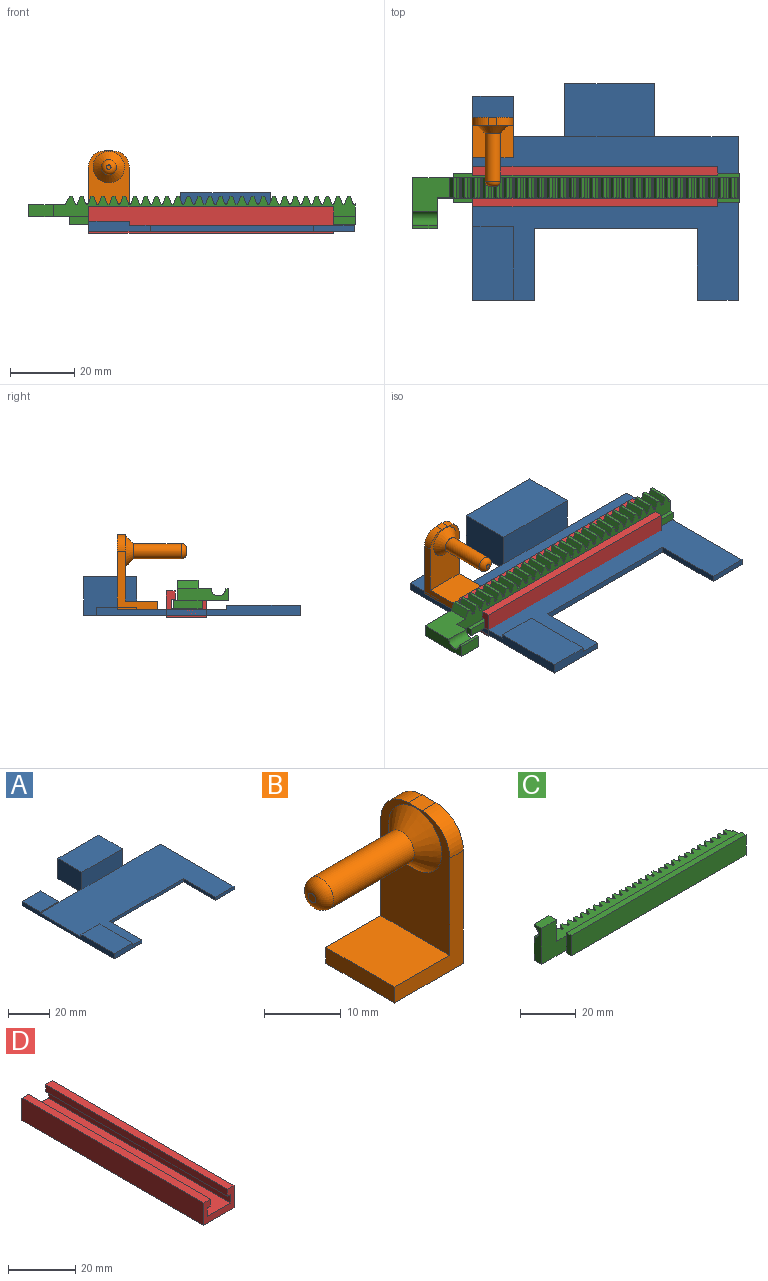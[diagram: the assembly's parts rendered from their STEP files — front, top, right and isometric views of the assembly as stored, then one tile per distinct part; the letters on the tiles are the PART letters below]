
ASSEMBLY  parts=4 mates=4
PART A: 23 faces, bbox 82.6x67.3x12.1 mm
  f0: plane 26.04x1.91mm, normal (0,1,0), area 49.6mm2, adj f2,f3,f15,f20
  f1: plane 19.05x3.18mm, normal (0,-1,0), area 52.4mm2, adj f2,f3,f5,f8,f9,f12
  f2: plane 82.55x50.8mm, normal (0,0,1), area 2774.2mm2, adj f0,f1,f4,f5,f6,f7,f8,f12
  f3: plane 82.55x67.31mm, normal (0,0,-1), area 3687.1mm2, adj f0,f1,f4,f5,f6,f10,f11,f12
  f4: plane 15.88x1.91mm, normal (0,1,0), area 30.2mm2, adj f2,f3,f10,f19
  f5: plane 63.5x3.18mm, normal (-1,0,0), area 158.1mm2, adj f1,f2,f3,f7,f9,f11,f16,f17
  f6: plane 12.7x1.91mm, normal (0,-1,0), area 24.2mm2, adj f2,f3,f13,f15
  f7: plane 12.7x1.27mm, normal (0,1,0), area 16.1mm2, adj f2,f5,f8,f9
  f8: plane 22.86x1.27mm, normal (1,0,0), area 29mm2, adj f1,f2,f7,f9
  f9: plane 22.86x12.7mm, normal (0,0,1), area 290.3mm2, adj f1,f5,f7,f8
  f10: plane 12.7x2.54mm, normal (1,0,0), area 32.3mm2, adj f3,f4,f11,f16,f17
  f11: plane 12.7x2.54mm, normal (0,1,0), area 32.3mm2, adj f3,f5,f10,f17
  f12: plane 22.23x1.91mm, normal (1,0,0), area 42.3mm2, adj f1,f2,f3,f14
  f13: plane 22.23x1.91mm, normal (-1,0,0), area 42.3mm2, adj f2,f3,f6,f14
  f14: plane 50.8x1.91mm, normal (0,-1,0), area 96.8mm2, adj f2,f3,f12,f13
  f15: plane 50.8x1.91mm, normal (1,0,0), area 96.8mm2, adj f0,f2,f3,f6
  f16: plane 12.7x0.64mm, normal (0,-1,0), area 8.1mm2, adj f2,f5,f10,f17
  f17: plane 12.7x12.7mm, normal (0,0,1), area 161.3mm2, adj f5,f10,f11,f16
  f18: plane 27.94x10.16mm, normal (0,-1,0), area 283.9mm2, adj f2,f19,f20,f22
  f19: plane 16.51x12.07mm, normal (-1,0,0), area 199.2mm2, adj f3,f4,f18,f21,f22
  f20: plane 16.51x12.07mm, normal (1,0,0), area 199.2mm2, adj f0,f3,f18,f21,f22
  f21: plane 27.94x12.07mm, normal (0,1,0), area 337.1mm2, adj f3,f19,f20,f22
  f22: plane 27.94x16.51mm, normal (0,0,1), area 461.3mm2, adj f18,f19,f20,f21
PART B: 14 faces, bbox 21.6x12.7x23.1 mm
  f0: plane 20.57x12.7mm, normal (-1,0,0), area 175.1mm2, adj f1,f5,f6,f7,f11,f12,f13
  f1: plane 12.7x10.16mm, normal (0,0,1), area 129mm2, adj f0,f2,f6,f7
  f2: plane 12.7x2.54mm, normal (-1,0,0), area 32.3mm2, adj f1,f3,f6,f7
  f3: plane 12.7x12.7mm, normal (0,0,-1), area 161.3mm2, adj f2,f4,f6,f7
  f4: plane 23.11x12.7mm, normal (1,0,0), area 282.5mm2, adj f3,f5,f6,f7,f11,f12
  f5: plane 2.54x2.54mm, normal (0,0,1), area 6.5mm2, adj f0,f4,f11,f12
  f6: plane 18.03x12.7mm, normal (0,-1,0), area 71.6mm2, adj f0,f1,f2,f3,f4,f12
  f7: plane 18.03x12.7mm, normal (0,1,0), area 71.6mm2, adj f0,f1,f2,f3,f4,f11
  f8: cylinder r=2.35mm len=14.86mm, axis (1,0,0), area 219.4mm2, adj f10,f13
  f9: plane 1.4x1.4mm, normal (-1,0,0), area 1.5mm2, adj f10
  f10: torus R=0.7mm, axis (-1,0,0), area 28.5mm2, adj f8,f9
  f11: cylinder r=5.08mm len=5.08mm, axis (-1,0,0), area 20.3mm2, adj f0,f4,f5,f7
  f12: cylinder r=5.08mm len=5.08mm, axis (1,0,0), area 20.3mm2, adj f0,f4,f5,f6
  f13: cone r=2.35mm half-angle=45deg, axis (1,0,0), area 81.7mm2, adj f0,f8
PART C: 178 faces, bbox 101.6x8.9x17.1 mm
  f0: plane 7.62x0.89mm, normal (0,1,0), area 6.8mm2, adj f172,f175,f176,f177
  f1: plane 6.35x0.89mm, normal (0,1,0), area 5.7mm2, adj f2,f3,f59,f173
  f2: plane 101.6x6.35mm, normal (0,0,-1), area 515.1mm2, adj f1,f4,f5,f6,f7,f8,f9,f10
  f3: plane 93.98x6.35mm, normal (0,0,1), area 486.1mm2, adj f1,f4,f5,f6,f7,f8,f9,f10
  f4: cylinder r=0.21mm len=6.35mm, axis (0,0,-1), area 1.6mm2, adj f2,f3,f59,f60
  f5: cylinder r=0.21mm len=6.35mm, axis (0,0,-1), area 1.6mm2, adj f2,f3,f60,f61
  f6: cylinder r=0.21mm len=6.35mm, axis (0,0,-1), area 1.6mm2, adj f2,f3,f63,f64
  f7: cylinder r=0.21mm len=6.35mm, axis (0,0,-1), area 1.6mm2, adj f2,f3,f64,f65
  f8: cylinder r=0.21mm len=6.35mm, axis (0,0,-1), area 1.6mm2, adj f2,f3,f67,f68
  f9: cylinder r=0.21mm len=6.35mm, axis (0,0,-1), area 1.6mm2, adj f2,f3,f68,f69
  f10: cylinder r=0.21mm len=6.35mm, axis (0,0,-1), area 1.6mm2, adj f2,f3,f71,f72
  f11: cylinder r=0.21mm len=6.35mm, axis (0,0,-1), area 1.6mm2, adj f2,f3,f72,f73
  f12: cylinder r=0.21mm len=6.35mm, axis (0,0,-1), area 1.6mm2, adj f2,f3,f75,f76
  f13: cylinder r=0.21mm len=6.35mm, axis (0,0,-1), area 1.6mm2, adj f2,f3,f76,f77
  f14: cylinder r=0.21mm len=6.35mm, axis (0,0,-1), area 1.6mm2, adj f2,f3,f79,f80
  f15: cylinder r=0.21mm len=6.35mm, axis (0,0,-1), area 1.6mm2, adj f2,f3,f80,f81
  f16: cylinder r=0.21mm len=6.35mm, axis (0,0,-1), area 1.6mm2, adj f2,f3,f83,f84
  f17: cylinder r=0.21mm len=6.35mm, axis (0,0,-1), area 1.6mm2, adj f2,f3,f84,f85
  f18: cylinder r=0.21mm len=6.35mm, axis (0,0,-1), area 1.6mm2, adj f2,f3,f87,f88
  f19: cylinder r=0.21mm len=6.35mm, axis (0,0,-1), area 1.6mm2, adj f2,f3,f88,f89
  f20: cylinder r=0.21mm len=6.35mm, axis (0,0,-1), area 1.6mm2, adj f2,f3,f91,f92
  f21: cylinder r=0.21mm len=6.35mm, axis (0,0,-1), area 1.6mm2, adj f2,f3,f92,f93
  f22: cylinder r=0.21mm len=6.35mm, axis (0,0,-1), area 1.6mm2, adj f2,f3,f95,f96
  f23: cylinder r=0.21mm len=6.35mm, axis (0,0,-1), area 1.6mm2, adj f2,f3,f96,f97
  f24: cylinder r=0.21mm len=6.35mm, axis (0,0,-1), area 1.6mm2, adj f2,f3,f99,f100
  f25: cylinder r=0.21mm len=6.35mm, axis (0,0,-1), area 1.6mm2, adj f2,f3,f100,f101
  f26: cylinder r=0.21mm len=6.35mm, axis (0,0,-1), area 1.6mm2, adj f2,f3,f103,f104
  f27: cylinder r=0.21mm len=6.35mm, axis (0,0,-1), area 1.6mm2, adj f2,f3,f104,f105
  f28: cylinder r=0.21mm len=6.35mm, axis (0,0,-1), area 1.6mm2, adj f2,f3,f107,f108
  f29: cylinder r=0.21mm len=6.35mm, axis (0,0,-1), area 1.6mm2, adj f2,f3,f108,f109
  f30: cylinder r=0.21mm len=6.35mm, axis (0,0,-1), area 1.6mm2, adj f2,f3,f111,f112
  f31: cylinder r=0.21mm len=6.35mm, axis (0,0,-1), area 1.6mm2, adj f2,f3,f112,f113
  f32: cylinder r=0.21mm len=6.35mm, axis (0,0,-1), area 1.6mm2, adj f2,f3,f115,f116
  f33: cylinder r=0.21mm len=6.35mm, axis (0,0,-1), area 1.6mm2, adj f2,f3,f116,f117
  f34: cylinder r=0.21mm len=6.35mm, axis (0,0,-1), area 1.6mm2, adj f2,f3,f119,f120
  f35: cylinder r=0.21mm len=6.35mm, axis (0,0,-1), area 1.6mm2, adj f2,f3,f120,f121
  f36: cylinder r=0.21mm len=6.35mm, axis (0,0,-1), area 1.6mm2, adj f2,f3,f123,f124
  f37: cylinder r=0.21mm len=6.35mm, axis (0,0,-1), area 1.6mm2, adj f2,f3,f124,f125
  f38: cylinder r=0.21mm len=6.35mm, axis (0,0,-1), area 1.6mm2, adj f2,f3,f127,f128
  f39: cylinder r=0.21mm len=6.35mm, axis (0,0,-1), area 1.6mm2, adj f2,f3,f128,f129
  f40: cylinder r=0.21mm len=6.35mm, axis (0,0,-1), area 1.6mm2, adj f2,f3,f131,f132
  f41: cylinder r=0.21mm len=6.35mm, axis (0,0,-1), area 1.6mm2, adj f2,f3,f132,f133
  f42: cylinder r=0.21mm len=6.35mm, axis (0,0,-1), area 1.6mm2, adj f2,f3,f135,f136
  f43: cylinder r=0.21mm len=6.35mm, axis (0,0,-1), area 1.6mm2, adj f2,f3,f136,f137
  f44: cylinder r=0.21mm len=6.35mm, axis (0,0,-1), area 1.6mm2, adj f2,f3,f139,f140
  f45: cylinder r=0.21mm len=6.35mm, axis (0,0,-1), area 1.6mm2, adj f2,f3,f140,f141
  f46: cylinder r=0.21mm len=6.35mm, axis (0,0,-1), area 1.6mm2, adj f2,f3,f143,f144
  f47: cylinder r=0.21mm len=6.35mm, axis (0,0,-1), area 1.6mm2, adj f2,f3,f144,f145
  f48: cylinder r=0.21mm len=6.35mm, axis (0,0,-1), area 1.6mm2, adj f2,f3,f147,f148
  f49: cylinder r=0.21mm len=6.35mm, axis (0,0,-1), area 1.6mm2, adj f2,f3,f148,f149
  f50: cylinder r=0.21mm len=6.35mm, axis (0,0,-1), area 1.6mm2, adj f2,f3,f151,f152
  f51: cylinder r=0.21mm len=6.35mm, axis (0,0,-1), area 1.6mm2, adj f2,f3,f152,f153
  f52: cylinder r=0.21mm len=6.35mm, axis (0,0,-1), area 1.6mm2, adj f2,f3,f155,f156
  f53: cylinder r=0.21mm len=6.35mm, axis (0,0,-1), area 1.6mm2, adj f2,f3,f156,f157
  f54: cylinder r=0.21mm len=6.35mm, axis (0,0,-1), area 1.6mm2, adj f2,f3,f159,f160
  f55: cylinder r=0.21mm len=6.35mm, axis (0,0,-1), area 1.6mm2, adj f2,f3,f160,f161
  f56: cylinder r=0.21mm len=6.35mm, axis (0,0,-1), area 1.6mm2, adj f2,f3,f163,f164
  f57: cylinder r=0.21mm len=6.35mm, axis (0,0,-1), area 1mm2, adj f2,f3,f164,f165
  f58: plane 8.89x2.54mm, normal (-1,0,0), area 22.6mm2, adj f166,f167,f168,f169,f170,f171
  f59: plane 6.35x2.24mm, normal (0.94,0.34,0), area 15.1mm2, adj f1,f2,f3,f4
  f60: plane 6.35x0.41mm, normal (0,1,0), area 2.6mm2, adj f2,f3,f4,f5
  f61: plane 6.35x2.24mm, normal (-0.94,0.34,0), area 15.1mm2, adj f2,f3,f5,f62
  f62: plane 6.35x0.89mm, normal (0,1,0), area 5.7mm2, adj f2,f3,f61,f63
  f63: plane 6.35x2.24mm, normal (0.94,0.34,0), area 15.1mm2, adj f2,f3,f6,f62
  f64: plane 6.35x0.41mm, normal (0,1,0), area 2.6mm2, adj f2,f3,f6,f7
  f65: plane 6.35x2.24mm, normal (-0.94,0.34,0), area 15.1mm2, adj f2,f3,f7,f66
  f66: plane 6.35x0.89mm, normal (0,1,0), area 5.7mm2, adj f2,f3,f65,f67
  f67: plane 6.35x2.24mm, normal (0.94,0.34,0), area 15.1mm2, adj f2,f3,f8,f66
  f68: plane 6.35x0.41mm, normal (0,1,0), area 2.6mm2, adj f2,f3,f8,f9
  f69: plane 6.35x2.24mm, normal (-0.94,0.34,0), area 15.1mm2, adj f2,f3,f9,f70
  f70: plane 6.35x0.89mm, normal (0,1,0), area 5.7mm2, adj f2,f3,f69,f71
  f71: plane 6.35x2.24mm, normal (0.94,0.34,0), area 15.1mm2, adj f2,f3,f10,f70
  f72: plane 6.35x0.41mm, normal (0,1,0), area 2.6mm2, adj f2,f3,f10,f11
  f73: plane 6.35x2.24mm, normal (-0.94,0.34,0), area 15.1mm2, adj f2,f3,f11,f74
  f74: plane 6.35x0.89mm, normal (0,1,0), area 5.7mm2, adj f2,f3,f73,f75
  f75: plane 6.35x2.24mm, normal (0.94,0.34,0), area 15.1mm2, adj f2,f3,f12,f74
  f76: plane 6.35x0.41mm, normal (0,1,0), area 2.6mm2, adj f2,f3,f12,f13
  f77: plane 6.35x2.24mm, normal (-0.94,0.34,0), area 15.1mm2, adj f2,f3,f13,f78
  f78: plane 6.35x0.89mm, normal (0,1,0), area 5.7mm2, adj f2,f3,f77,f79
  f79: plane 6.35x2.24mm, normal (0.94,0.34,0), area 15.1mm2, adj f2,f3,f14,f78
  f80: plane 6.35x0.41mm, normal (0,1,0), area 2.6mm2, adj f2,f3,f14,f15
  f81: plane 6.35x2.24mm, normal (-0.94,0.34,0), area 15.1mm2, adj f2,f3,f15,f82
  f82: plane 6.35x0.89mm, normal (0,1,0), area 5.7mm2, adj f2,f3,f81,f83
  f83: plane 6.35x2.24mm, normal (0.94,0.34,0), area 15.1mm2, adj f2,f3,f16,f82
  f84: plane 6.35x0.41mm, normal (0,1,0), area 2.6mm2, adj f2,f3,f16,f17
  f85: plane 6.35x2.24mm, normal (-0.94,0.34,0), area 15.1mm2, adj f2,f3,f17,f86
  f86: plane 6.35x0.89mm, normal (0,1,0), area 5.7mm2, adj f2,f3,f85,f87
  f87: plane 6.35x2.24mm, normal (0.94,0.34,0), area 15.1mm2, adj f2,f3,f18,f86
  f88: plane 6.35x0.41mm, normal (0,1,0), area 2.6mm2, adj f2,f3,f18,f19
  f89: plane 6.35x2.24mm, normal (-0.94,0.34,0), area 15.1mm2, adj f2,f3,f19,f90
  f90: plane 6.35x0.89mm, normal (0,1,0), area 5.7mm2, adj f2,f3,f89,f91
  f91: plane 6.35x2.24mm, normal (0.94,0.34,0), area 15.1mm2, adj f2,f3,f20,f90
  f92: plane 6.35x0.41mm, normal (0,1,0), area 2.6mm2, adj f2,f3,f20,f21
  f93: plane 6.35x2.24mm, normal (-0.94,0.34,0), area 15.1mm2, adj f2,f3,f21,f94
  f94: plane 6.35x0.89mm, normal (0,1,0), area 5.7mm2, adj f2,f3,f93,f95
  f95: plane 6.35x2.24mm, normal (0.94,0.34,0), area 15.1mm2, adj f2,f3,f22,f94
  f96: plane 6.35x0.41mm, normal (0,1,0), area 2.6mm2, adj f2,f3,f22,f23
  f97: plane 6.35x2.24mm, normal (-0.94,0.34,0), area 15.1mm2, adj f2,f3,f23,f98
  f98: plane 6.35x0.89mm, normal (0,1,0), area 5.7mm2, adj f2,f3,f97,f99
  f99: plane 6.35x2.24mm, normal (0.94,0.34,0), area 15.1mm2, adj f2,f3,f24,f98
  f100: plane 6.35x0.41mm, normal (0,1,0), area 2.6mm2, adj f2,f3,f24,f25
  f101: plane 6.35x2.24mm, normal (-0.94,0.34,0), area 15.1mm2, adj f2,f3,f25,f102
  f102: plane 6.35x0.89mm, normal (0,1,0), area 5.7mm2, adj f2,f3,f101,f103
  f103: plane 6.35x2.24mm, normal (0.94,0.34,0), area 15.1mm2, adj f2,f3,f26,f102
  f104: plane 6.35x0.41mm, normal (0,1,0), area 2.6mm2, adj f2,f3,f26,f27
  f105: plane 6.35x2.24mm, normal (-0.94,0.34,0), area 15.1mm2, adj f2,f3,f27,f106
  f106: plane 6.35x0.89mm, normal (0,1,0), area 5.7mm2, adj f2,f3,f105,f107
  f107: plane 6.35x2.24mm, normal (0.94,0.34,0), area 15.1mm2, adj f2,f3,f28,f106
  f108: plane 6.35x0.41mm, normal (0,1,0), area 2.6mm2, adj f2,f3,f28,f29
  f109: plane 6.35x2.24mm, normal (-0.94,0.34,0), area 15.1mm2, adj f2,f3,f29,f110
  f110: plane 6.35x0.89mm, normal (0,1,0), area 5.7mm2, adj f2,f3,f109,f111
  f111: plane 6.35x2.24mm, normal (0.94,0.34,0), area 15.1mm2, adj f2,f3,f30,f110
  f112: plane 6.35x0.41mm, normal (0,1,0), area 2.6mm2, adj f2,f3,f30,f31
  f113: plane 6.35x2.24mm, normal (-0.94,0.34,0), area 15.1mm2, adj f2,f3,f31,f114
  f114: plane 6.35x0.89mm, normal (0,1,0), area 5.7mm2, adj f2,f3,f113,f115
  f115: plane 6.35x2.24mm, normal (0.94,0.34,0), area 15.1mm2, adj f2,f3,f32,f114
  f116: plane 6.35x0.41mm, normal (0,1,0), area 2.6mm2, adj f2,f3,f32,f33
  f117: plane 6.35x2.24mm, normal (-0.94,0.34,0), area 15.1mm2, adj f2,f3,f33,f118
  f118: plane 6.35x0.89mm, normal (0,1,0), area 5.7mm2, adj f2,f3,f117,f119
  f119: plane 6.35x2.24mm, normal (0.94,0.34,0), area 15.1mm2, adj f2,f3,f34,f118
  f120: plane 6.35x0.41mm, normal (0,1,0), area 2.6mm2, adj f2,f3,f34,f35
  f121: plane 6.35x2.24mm, normal (-0.94,0.34,0), area 15.1mm2, adj f2,f3,f35,f122
  f122: plane 6.35x0.89mm, normal (0,1,0), area 5.7mm2, adj f2,f3,f121,f123
  f123: plane 6.35x2.24mm, normal (0.94,0.34,0), area 15.1mm2, adj f2,f3,f36,f122
  f124: plane 6.35x0.41mm, normal (0,1,0), area 2.6mm2, adj f2,f3,f36,f37
  f125: plane 6.35x2.24mm, normal (-0.94,0.34,0), area 15.1mm2, adj f2,f3,f37,f126
  f126: plane 6.35x0.89mm, normal (0,1,0), area 5.7mm2, adj f2,f3,f125,f127
  f127: plane 6.35x2.24mm, normal (0.94,0.34,0), area 15.1mm2, adj f2,f3,f38,f126
  f128: plane 6.35x0.41mm, normal (0,1,0), area 2.6mm2, adj f2,f3,f38,f39
  f129: plane 6.35x2.24mm, normal (-0.94,0.34,0), area 15.1mm2, adj f2,f3,f39,f130
  f130: plane 6.35x0.89mm, normal (0,1,0), area 5.7mm2, adj f2,f3,f129,f131
  f131: plane 6.35x2.24mm, normal (0.94,0.34,0), area 15.1mm2, adj f2,f3,f40,f130
  f132: plane 6.35x0.41mm, normal (0,1,0), area 2.6mm2, adj f2,f3,f40,f41
  f133: plane 6.35x2.24mm, normal (-0.94,0.34,0), area 15.1mm2, adj f2,f3,f41,f134
  f134: plane 6.35x0.89mm, normal (0,1,0), area 5.7mm2, adj f2,f3,f133,f135
  f135: plane 6.35x2.24mm, normal (0.94,0.34,0), area 15.1mm2, adj f2,f3,f42,f134
  f136: plane 6.35x0.41mm, normal (0,1,0), area 2.6mm2, adj f2,f3,f42,f43
  f137: plane 6.35x2.24mm, normal (-0.94,0.34,0), area 15.1mm2, adj f2,f3,f43,f138
  f138: plane 6.35x0.89mm, normal (0,1,0), area 5.7mm2, adj f2,f3,f137,f139
  f139: plane 6.35x2.24mm, normal (0.94,0.34,0), area 15.1mm2, adj f2,f3,f44,f138
  f140: plane 6.35x0.41mm, normal (0,1,0), area 2.6mm2, adj f2,f3,f44,f45
  f141: plane 6.35x2.24mm, normal (-0.94,0.34,0), area 15.1mm2, adj f2,f3,f45,f142
  f142: plane 6.35x0.89mm, normal (0,1,0), area 5.7mm2, adj f2,f3,f141,f143
  f143: plane 6.35x2.24mm, normal (0.94,0.34,0), area 15.1mm2, adj f2,f3,f46,f142
  f144: plane 6.35x0.41mm, normal (0,1,0), area 2.6mm2, adj f2,f3,f46,f47
  f145: plane 6.35x2.24mm, normal (-0.94,0.34,0), area 15.1mm2, adj f2,f3,f47,f146
  f146: plane 6.35x0.89mm, normal (0,1,0), area 5.7mm2, adj f2,f3,f145,f147
  f147: plane 6.35x2.24mm, normal (0.94,0.34,0), area 15.1mm2, adj f2,f3,f48,f146
  f148: plane 6.35x0.41mm, normal (0,1,0), area 2.6mm2, adj f2,f3,f48,f49
  f149: plane 6.35x2.24mm, normal (-0.94,0.34,0), area 15.1mm2, adj f2,f3,f49,f150
  f150: plane 6.35x0.89mm, normal (0,1,0), area 5.7mm2, adj f2,f3,f149,f151
  f151: plane 6.35x2.24mm, normal (0.94,0.34,0), area 15.1mm2, adj f2,f3,f50,f150
  f152: plane 6.35x0.41mm, normal (0,1,0), area 2.6mm2, adj f2,f3,f50,f51
  f153: plane 6.35x2.24mm, normal (-0.94,0.34,0), area 15.1mm2, adj f2,f3,f51,f154
  f154: plane 6.35x0.89mm, normal (0,1,0), area 5.7mm2, adj f2,f3,f153,f155
  f155: plane 6.35x2.24mm, normal (0.94,0.34,0), area 15.1mm2, adj f2,f3,f52,f154
  f156: plane 6.35x0.41mm, normal (0,1,0), area 2.6mm2, adj f2,f3,f52,f53
  f157: plane 6.35x2.24mm, normal (-0.94,0.34,0), area 15.1mm2, adj f2,f3,f53,f158
  f158: plane 6.35x0.89mm, normal (0,1,0), area 5.7mm2, adj f2,f3,f157,f159
  f159: plane 6.35x2.24mm, normal (0.94,0.34,0), area 15.1mm2, adj f2,f3,f54,f158
  f160: plane 6.35x0.41mm, normal (0,1,0), area 2.6mm2, adj f2,f3,f54,f55
  f161: plane 6.35x2.24mm, normal (-0.94,0.34,0), area 15.1mm2, adj f2,f3,f55,f162
  f162: plane 6.35x0.89mm, normal (0,1,0), area 5.7mm2, adj f2,f3,f161,f163
  f163: plane 6.35x2.24mm, normal (0.94,0.34,0), area 15.1mm2, adj f2,f3,f56,f162
  f164: plane 6.35x0.41mm, normal (0,1,0), area 2.6mm2, adj f2,f3,f56,f57
  f165: plane 8.89x6.57mm, normal (1,0,0), area 48.1mm2, adj f2,f3,f57,f166,f167,f168,f169,f170
  f166: plane 88.9x1.27mm, normal (0,1,0), area 112.9mm2, adj f2,f58,f165,f167
  f167: plane 88.9x2.54mm, normal (0,0,-1), area 225.8mm2, adj f58,f165,f166,f168
  f168: plane 88.9x8.89mm, normal (0,-1,0), area 790.3mm2, adj f58,f165,f167,f169
  f169: plane 88.9x2.54mm, normal (0,0,1), area 225.8mm2, adj f58,f165,f168,f170
  f170: plane 88.9x1.27mm, normal (0,1,0), area 112.9mm2, adj f3,f58,f165,f169
  f171: plane 15.88x12.7mm, normal (0,-1,0), area 153.2mm2, adj f2,f3,f58,f172,f175,f176
  f172: plane 15.88x3.81mm, normal (-1,0,0), area 52.3mm2, adj f0,f2,f171,f174,f176,f177
  f173: plane 6.35x2.54mm, normal (-0.89,0.45,0), area 18mm2, adj f1,f2,f3,f174
  f174: plane 11.43x10.41mm, normal (0,1,0), area 103.5mm2, adj f2,f3,f172,f173,f175,f177
  f175: plane 9.53x3.81mm, normal (1,0,0), area 28.1mm2, adj f0,f3,f171,f174,f176,f177
  f176: plane 7.62x3.81mm, normal (0,0,1), area 29mm2, adj f0,f171,f172,f175
  f177: cylinder r=2.29mm len=7.62mm, axis (-1,0,0), area 54.7mm2, adj f0,f172,f174,f175
PART D: 14 faces, bbox 12.7x76.2x8.1 mm
  f0: plane 76.2x3.05mm, normal (1,0,0), area 232.3mm2, adj f1,f11,f12,f13
  f1: plane 76.2x1.27mm, normal (0,0,-1), area 96.8mm2, adj f0,f2,f12,f13
  f2: plane 76.2x2.54mm, normal (1,0,0), area 193.5mm2, adj f1,f3,f12,f13
  f3: plane 76.2x2.79mm, normal (0,0,1), area 212.9mm2, adj f2,f4,f12,f13
  f4: plane 76.2x8.13mm, normal (-1,0,0), area 619.4mm2, adj f3,f5,f12,f13
  f5: plane 76.2x12.7mm, normal (0,0,-1), area 967.7mm2, adj f4,f6,f12,f13
  f6: plane 76.2x8.13mm, normal (1,0,0), area 619.4mm2, adj f5,f7,f12,f13
  f7: plane 76.2x2.79mm, normal (0,0,1), area 212.9mm2, adj f6,f8,f12,f13
  f8: plane 76.2x2.54mm, normal (-1,0,0), area 193.5mm2, adj f7,f9,f12,f13
  f9: plane 76.2x1.27mm, normal (0,0,-1), area 96.8mm2, adj f8,f10,f12,f13
  f10: plane 76.2x3.05mm, normal (-1,0,0), area 232.3mm2, adj f9,f11,f12,f13
  f11: plane 76.2x9.65mm, normal (0,0,1), area 735.5mm2, adj f0,f10,f12,f13
  f12: plane 12.7x8.13mm, normal (0,-1,0), area 55.7mm2, adj f0,f1,f2,f3,f4,f5,f6,f7
  f13: plane 12.7x8.13mm, normal (0,1,0), area 55.7mm2, adj f0,f1,f2,f3,f4,f5,f6,f7
PLACE A rot(axis=(0,0,1),0deg) t=(-37.21,-9.77,-3.28)mm
PLACE B rot(axis=(0,0,1),90deg) t=(-31.01,9.08,-1.38)mm
PLACE C rot(axis=(1,0,0),90deg) t=(109.18,-0.21,1.24)mm
PLACE D rot(axis=(0,0,1),90deg) t=(0.89,0.17,-3.84)mm fixed
MATE planar C.f3 <-> D.f2  axis (0,-1,0) through (-0.88,-3.38,3.92)mm
MATE planar C.f168 <-> D.f11  axis (0,0,-1) through (1.23,-0.21,-1.3)mm
MATE planar D.f13 <-> A.f5  axis (-1,0,0) through (-37.21,0.17,-0.68)mm
MATE planar B.f3 <-> A.f2  axis (0,0,-1) through (-24.66,15.43,-1.38)mm
